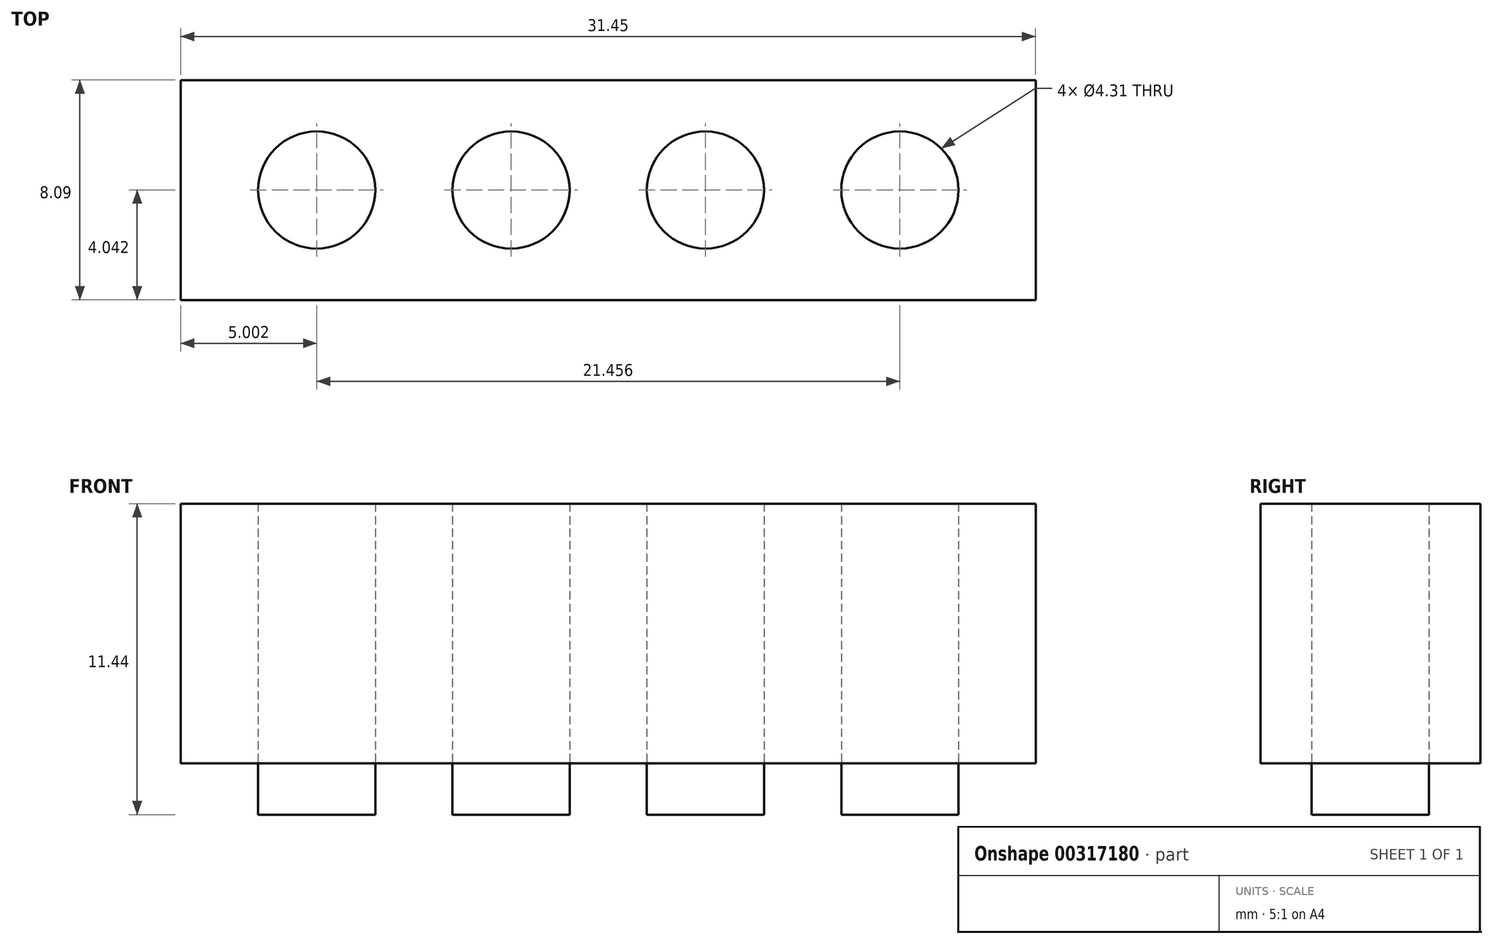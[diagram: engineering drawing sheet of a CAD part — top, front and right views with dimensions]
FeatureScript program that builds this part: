
annotation { "Feature Type Name" : "Feature", "Feature Type Description" : "" }
export const myFeature = defineFeature(function(context is Context, id is Id, definition is map)
    precondition{}
    {
        {
            var Q0;
            Q0=qCreatedBy(makeId("Top.planeOp"),FACE);
            var sketch = newSketch(context, id + "F0", { "sketchPlane" : qUnion([Q0])});
            skLineSegment(sketch, "E0.bottom", {"start": v(-10.45, 20.82) * mm, "end": v(21, 20.82) * mm});
            skLineSegment(sketch, "E0.top", {"start": v(-10.45, 12.73) * mm, "end": v(21, 12.73) * mm});
            skLineSegment(sketch, "E0.left", {"start": v(-10.45, 20.82) * mm, "end": v(-10.45, 12.73) * mm});
            skLineSegment(sketch, "E0.right", {"start": v(21, 20.82) * mm, "end": v(21, 12.73) * mm});
            skCircle(sketch, "E1", {"center": v(-5.45, 16.77) * mm, "radius": 2.15 * mm});
            skCircle(sketch, "E2", {"center": v(16, 16.77) * mm, "radius": 2.16 * mm});
            skCircle(sketch, "E3", {"center": v(8.86, 16.77) * mm, "radius": 2.15 * mm});
            skCircle(sketch, "E4", {"center": v(1.7, 16.77) * mm, "radius": 2.15 * mm});
            skSolve(sketch);
        }
        {
            var Q0;
            Q0=makeQuery(id+"F0.imprint","IMPRINT",FACE,{"disambiguationData":[TD([[makeQuery(id+"F0.imprint","IMPRINT",EDGE,{"derivedFrom":sQuery(id+"F0.wireOp",EDGE,"E4")}),1.0]])]});
            var Q1;
            Q1=makeQuery(id+"F0.imprint","IMPRINT",FACE,{"disambiguationData":[TD([[makeQuery(id+"F0.imprint","IMPRINT",EDGE,{"derivedFrom":sQuery(id+"F0.wireOp",EDGE,"E3")}),1.0]])]});
            var Q2;
            Q2=makeQuery(id+"F0.imprint","IMPRINT",FACE,{"disambiguationData":[TD([[makeQuery(id+"F0.imprint","IMPRINT",EDGE,{"derivedFrom":sQuery(id+"F0.wireOp",EDGE,"E2")}),1.0]])]});
            var Q3;
            Q3=makeQuery(id+"F0.imprint","IMPRINT",FACE,{"disambiguationData":[TD([[makeQuery(id+"F0.imprint","IMPRINT",EDGE,{"derivedFrom":sQuery(id+"F0.wireOp",EDGE,"E1")}),1.0]])]});
            extrude(context, id + "F1", {"entities" : qUnion([Q0, Q1, Q2, Q3]), "oppositeDirection" : true, "depth" : 1.89 * mm});
        }
        {
            var Q0;
            Q0=makeQuery(id+"F0.imprint","IMPRINT",FACE,{"disambiguationData":[TD([[makeQuery(id+"F0.imprint","IMPRINT",EDGE,{"derivedFrom":sQuery(id+"F0.wireOp",EDGE,"E0.bottom")}),-1.0]])]});
            extrude(context, id + "F2", {"entities" : qUnion([Q0]), "depth" : 9.55 * mm});
        }
    });
